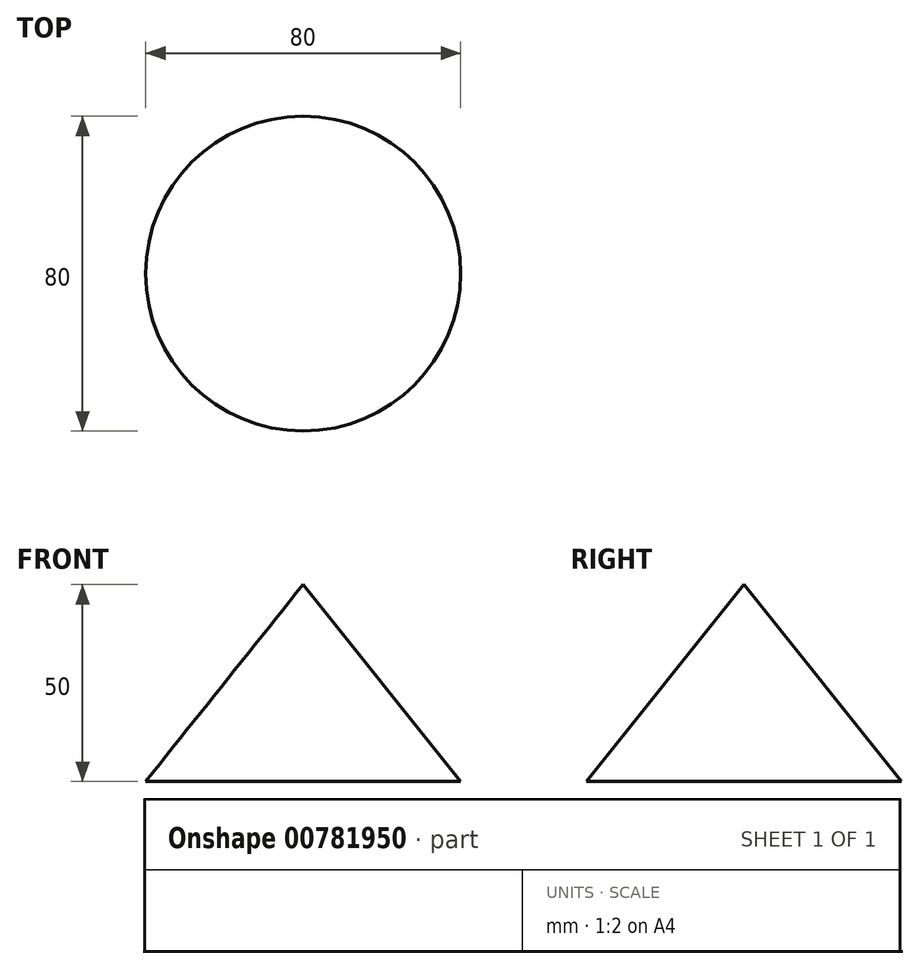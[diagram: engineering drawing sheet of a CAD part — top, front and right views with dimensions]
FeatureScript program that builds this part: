
annotation { "Feature Type Name" : "Feature", "Feature Type Description" : "" }
export const myFeature = defineFeature(function(context is Context, id is Id, definition is map)
    precondition{}
    {
        {
            var Q0;
            Q0=qCreatedBy(makeId("Front.planeOp"),FACE);
            var sketch = newSketch(context, id + "F0", { "sketchPlane" : qUnion([Q0])});
            skLineSegment(sketch, "E0", {"start": v(40, 0) * mm, "end": v(0, 0) * mm});
            skLineSegment(sketch, "E1", {"start": v(0, 0) * mm, "end": v(0, 50) * mm});
            skLineSegment(sketch, "E2", {"start": v(0, 50) * mm, "end": v(40, 0) * mm});
            skSolve(sketch);
        }
        {
            var Q0;
            Q0=makeQuery(id+"F0.imprint","IMPRINT",FACE,{"disambiguationData":[TD([[makeQuery(id+"F0.imprint","IMPRINT",EDGE,{"derivedFrom":sQuery(id+"F0.wireOp",EDGE,"E0")}),-1.0]])]});
            var Q1;
            Q1=sQuery(id+"F0.wireOp",EDGE,"E1");
            revolve(context, id + "F1", {"surfaceOperationType" : NewSurfaceOperationType.NEW, "entities" : qUnion([Q0]), "axis" : qUnion([Q1]), "revolveType" : RevolveType.FULL});
        }
    });
